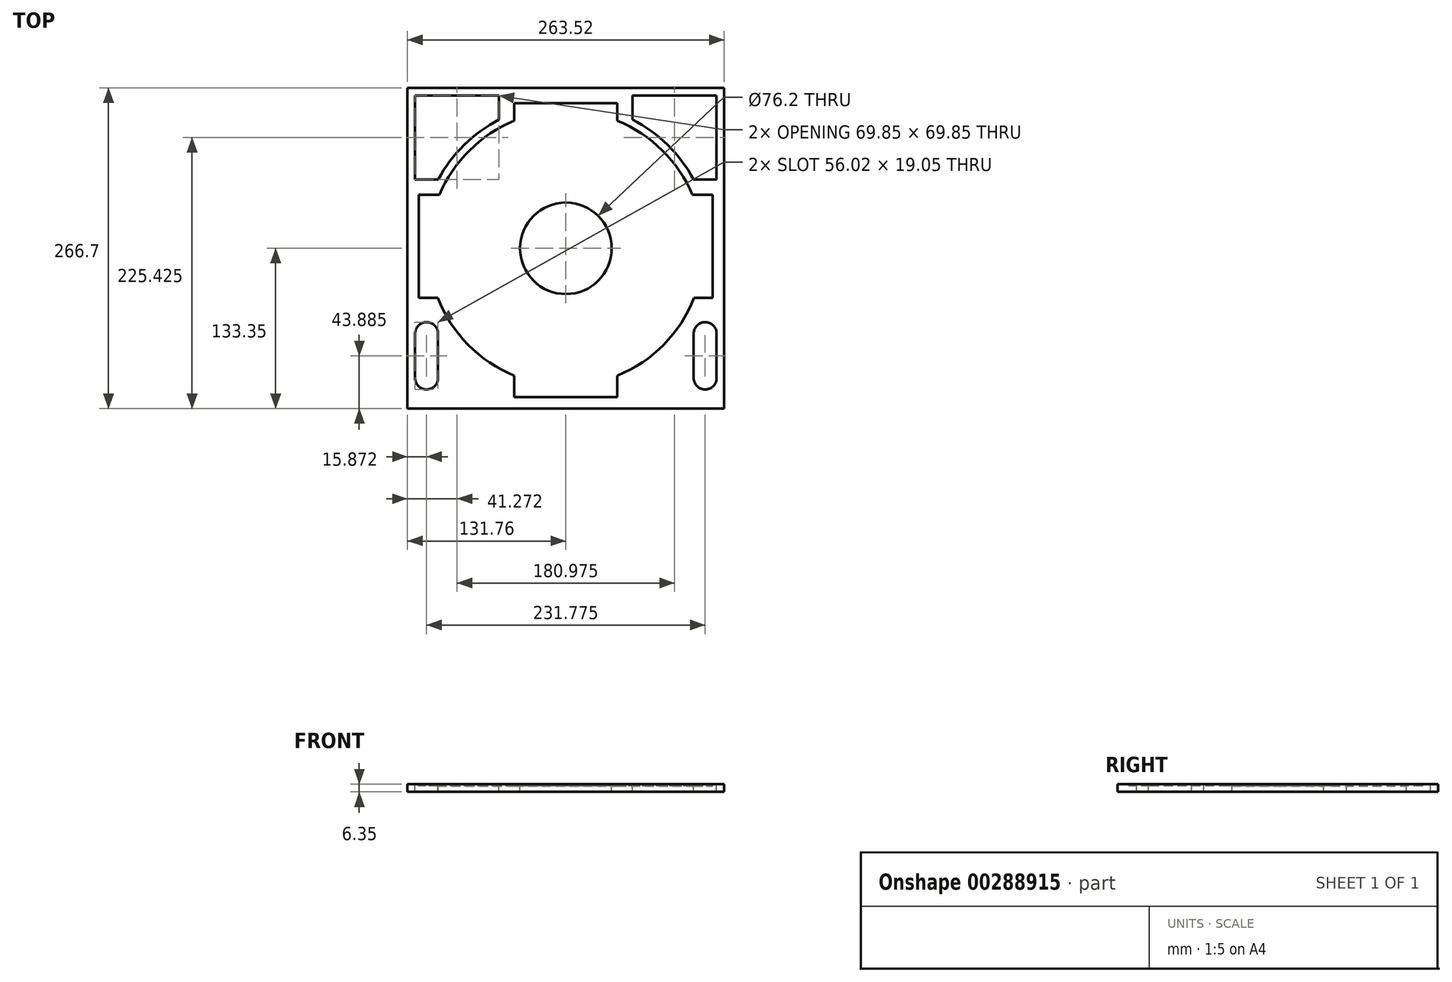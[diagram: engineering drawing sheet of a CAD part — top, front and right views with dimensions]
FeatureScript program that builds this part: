
annotation { "Feature Type Name" : "Feature", "Feature Type Description" : "" }
export const myFeature = defineFeature(function(context is Context, id is Id, definition is map)
    precondition{}
    {
        {
            var Q0;
            Q0=qCreatedBy(makeId("Top.planeOp"),FACE);
            var sketch = newSketch(context, id + "F0", { "sketchPlane" : qUnion([Q0])});
            skLineSegment(sketch, "E0.bottom", {"start": v(-134.94, -136.53) * mm, "end": v(134.94, -136.53) * mm});
            skLineSegment(sketch, "E0.top", {"start": v(-134.94, 136.53) * mm, "end": v(134.94, 136.53) * mm});
            skLineSegment(sketch, "E0.left", {"start": v(-134.94, -136.53) * mm, "end": v(-134.94, 136.53) * mm});
            skLineSegment(sketch, "E0.right", {"start": v(134.94, -136.53) * mm, "end": v(134.94, 136.53) * mm});
            skPoint(sketch, "E0.middle", {"position": v(0, 0) * mm});
            skSolve(sketch);
        }
        {
            var Q0;
            Q0 = qSketchRegion(id + "F0", true);
            extrude(context, id + "F1", {"entities" : qUnion([Q0]), "depth" : 6.35 * mm});
        }
        {
            var Q0;
            Q0=makeQuery(id+"F1.opExtrude","CAP_FACE",FACE,{"disambiguationData":[OSD([sQuery(id+"F0.wireOp",EDGE,"E0.bottom"),sQuery(id+"F0.wireOp",EDGE,"E0.top"),sQuery(id+"F0.wireOp",EDGE,"E0.left"),sQuery(id+"F0.wireOp",EDGE,"E0.right")])],"isStart":false});
            var sketch = newSketch(context, id + "F2", { "sketchPlane" : qUnion([Q0])});
            skLineSegment(sketch, "E1", {"start": v(-125.41, 136.53) * mm, "end": v(-125.41, -136.53) * mm, "construction": true});
            skLineSegment(sketch, "E2", {"start": v(125.41, 136.53) * mm, "end": v(125.41, -136.53) * mm, "construction": true});
            skLineSegment(sketch, "E3", {"start": v(-134.94, 127) * mm, "end": v(134.94, 127) * mm, "construction": true});
            skLineSegment(sketch, "E4", {"start": v(-134.94, -117.48) * mm, "end": v(134.94, -117.48) * mm, "construction": true});
            skLineSegment(sketch, "E5", {"start": v(-134.94, 136.53) * mm, "end": v(134.94, -136.53) * mm, "construction": true});
            skLineSegment(sketch, "E6", {"start": v(134.94, -107.94) * mm, "end": v(125.41, -107.94) * mm, "construction": true});
            skLineSegment(sketch, "E7", {"start": v(134.94, -71) * mm, "end": v(125.41, -71) * mm, "construction": true});
            skLineSegment(sketch, "E8", {"start": v(-134.94, -61.46) * mm, "end": v(134.94, -61.46) * mm, "construction": true});
            skLineSegment(sketch, "E9", {"start": v(-125.41, 127) * mm, "end": v(-125.41, 57.15) * mm});
            skLineSegment(sketch, "E10", {"start": v(-125.41, 57.15) * mm, "end": v(-106.25, 57.15) * mm});
            skLineSegment(sketch, "E11", {"start": v(-125.41, 127) * mm, "end": v(-55.56, 127) * mm});
            skLineSegment(sketch, "E12", {"start": v(-55.56, 127) * mm, "end": v(-55.56, 107.09) * mm});
            skLineSegment(sketch, "E13", {"start": v(55.56, 107.09) * mm, "end": v(55.56, 127) * mm});
            skLineSegment(sketch, "E14", {"start": v(55.56, 127) * mm, "end": v(125.41, 127) * mm});
            skLineSegment(sketch, "E15", {"start": v(125.41, 127) * mm, "end": v(125.41, 57.15) * mm});
            skLineSegment(sketch, "E16", {"start": v(125.41, 57.15) * mm, "end": v(106.25, 57.15) * mm});
            skArc(sketch, "E17.trimOffspring", {"start": v(106.25, 57.15) * mm, "mid": v(84.67, 85.94) * mm, "end": v(55.56, 107.09) * mm});
            skArc(sketch, "E18.trimOffspring", {"start": v(-55.56, 107.09) * mm, "mid": v(-84.67, 85.94) * mm, "end": v(-106.25, 57.15) * mm});
            skLineSegment(sketch, "E19", {"start": v(-106.36, 136.53) * mm, "end": v(-106.36, -136.53) * mm, "construction": true});
            skLineSegment(sketch, "E20", {"start": v(106.36, 136.53) * mm, "end": v(106.36, -136.53) * mm, "construction": true});
            skLineSegment(sketch, "E21", {"start": v(-125.41, -71) * mm, "end": v(-125.41, -107.94) * mm});
            skLineSegment(sketch, "E22", {"start": v(-106.36, -107.94) * mm, "end": v(-106.36, -71) * mm});
            skArc(sketch, "E23", {"start": v(-106.36, -71.49) * mm, "mid": v(-115.89, -61.46) * mm, "end": v(-125.41, -71.49) * mm});
            skArc(sketch, "E24", {"start": v(-125.41, -107.45) * mm, "mid": v(-115.89, -117.48) * mm, "end": v(-106.36, -107.45) * mm});
            skLineSegment(sketch, "E25.trimOffspring", {"start": v(-125.41, -71) * mm, "end": v(-134.94, -71) * mm, "construction": true});
            skLineSegment(sketch, "E26.trimOffspring", {"start": v(-125.41, -107.94) * mm, "end": v(-134.94, -107.94) * mm, "construction": true});
            skLineSegment(sketch, "E27", {"start": v(106.36, -71) * mm, "end": v(106.36, -107.94) * mm});
            skLineSegment(sketch, "E28", {"start": v(106.36, -107.94) * mm, "end": v(106.68, -107.94) * mm});
            skLineSegment(sketch, "E29", {"start": v(125.41, -107.94) * mm, "end": v(125.41, -71) * mm});
            skArc(sketch, "E30", {"start": v(125.41, -71.48) * mm, "mid": v(115.89, -61.46) * mm, "end": v(106.36, -71.48) * mm});
            skArc(sketch, "E31", {"start": v(106.36, -107.45) * mm, "mid": v(115.89, -117.48) * mm, "end": v(125.41, -107.45) * mm});
            skLineSegment(sketch, "E32.trimOffspring", {"start": v(106.36, -71) * mm, "end": v(-106.36, -71) * mm, "construction": true});
            skLineSegment(sketch, "E33.trimOffspring", {"start": v(106.68, -107.94) * mm, "end": v(-106.36, -107.94) * mm, "construction": true});
            skSolve(sketch);
        }
        {
            var Q0;
            Q0 = qSketchRegion(id + "F2", true);
            extrude(context, id + "F3", {"entities" : qUnion([Q0]), "operationType" : NewBodyOperationType.REMOVE, "endBound" : BoundingType.UP_TO_NEXT, "oppositeDirection" : true, "depth" : 25.4 * mm});
        }
        {
            var Q0;
            Q0=makeQuery(id+"F1.opExtrude","CAP_FACE",FACE,{"disambiguationData":[OSD([sQuery(id+"F0.wireOp",EDGE,"E0.bottom"),sQuery(id+"F0.wireOp",EDGE,"E0.top"),sQuery(id+"F0.wireOp",EDGE,"E0.left"),sQuery(id+"F0.wireOp",EDGE,"E0.right")])],"isStart":false});
            var sketch = newSketch(context, id + "F4", { "sketchPlane" : qUnion([Q0])});
            skLineSegment(sketch, "E34", {"start": v(-134.94, 136.53) * mm, "end": v(134.94, -136.53) * mm, "construction": true});
            skCircle(sketch, "E35", {"center": v(0, 0) * mm, "radius": 38.1 * mm});
            skSolve(sketch);
        }
        {
            var Q0;
            Q0 = qSketchRegion(id + "F4", true);
            extrude(context, id + "F5", {"entities" : qUnion([Q0]), "operationType" : NewBodyOperationType.REMOVE, "endBound" : BoundingType.UP_TO_NEXT, "oppositeDirection" : true, "depth" : 25.4 * mm});
        }
        {
            var Q0;
            Q0=makeQuery(id+"F1.opExtrude","CAP_FACE",FACE,{"disambiguationData":[OSD([sQuery(id+"F0.wireOp",EDGE,"E0.bottom"),sQuery(id+"F0.wireOp",EDGE,"E0.top"),sQuery(id+"F0.wireOp",EDGE,"E0.left"),sQuery(id+"F0.wireOp",EDGE,"E0.right")])],"isStart":false});
            var sketch = newSketch(context, id + "F6", { "sketchPlane" : qUnion([Q0])});
            skLineSegment(sketch, "E36", {"start": v(-134.94, 136.53) * mm, "end": v(134.94, -136.53) * mm, "construction": true});
            skCircle(sketch, "E37", {"center": v(0, 0) * mm, "radius": 114.3 * mm});
            skLineSegment(sketch, "E38", {"start": v(0, 136.53) * mm, "end": v(0, -136.53) * mm, "construction": true});
            skLineSegment(sketch, "E39", {"start": v(-134.94, 0) * mm, "end": v(134.94, 0) * mm, "construction": true});
            skLineSegment(sketch, "E40", {"start": v(-55.56, 136.53) * mm, "end": v(-55.56, -136.53) * mm, "construction": true});
            skLineSegment(sketch, "E41", {"start": v(55.56, 136.53) * mm, "end": v(55.56, -136.53) * mm, "construction": true});
            skLineSegment(sketch, "E42", {"start": v(-134.94, 57.15) * mm, "end": v(134.94, 57.15) * mm, "construction": true});
            skLineSegment(sketch, "E43", {"start": v(-106.59, -41.28) * mm, "end": v(-42.86, -41.28) * mm, "construction": true});
            skLineSegment(sketch, "E44", {"start": v(-42.86, 136.53) * mm, "end": v(-42.86, 43.37) * mm, "construction": true});
            skLineSegment(sketch, "E45", {"start": v(42.86, 136.53) * mm, "end": v(42.86, 44.45) * mm, "construction": true});
            skLineSegment(sketch, "E46", {"start": v(-134.94, 127) * mm, "end": v(134.94, 127) * mm, "construction": true});
            skLineSegment(sketch, "E47", {"start": v(134.94, 120.65) * mm, "end": v(-134.94, 120.65) * mm, "construction": true});
            skLineSegment(sketch, "E48", {"start": v(-134.94, -123.83) * mm, "end": v(134.94, -123.83) * mm, "construction": true});
            skLineSegment(sketch, "E49.bottom", {"start": v(-42.86, 120.65) * mm, "end": v(42.86, 120.65) * mm});
            skLineSegment(sketch, "E49.top", {"start": v(-42.86, -123.83) * mm, "end": v(42.86, -123.83) * mm});
            skLineSegment(sketch, "E49.left", {"start": v(-42.86, 120.65) * mm, "end": v(-42.86, 44.45) * mm});
            skLineSegment(sketch, "E49.right", {"start": v(42.86, 120.65) * mm, "end": v(42.86, 44.45) * mm});
            skLineSegment(sketch, "E50", {"start": v(-105.3, 44.45) * mm, "end": v(-42.86, 44.45) * mm, "construction": true});
            skLineSegment(sketch, "E51.bottom", {"start": v(-105.3, 44.45) * mm, "end": v(-42.86, 44.45) * mm});
            skLineSegment(sketch, "E51.top", {"start": v(-106.59, -41.28) * mm, "end": v(-42.86, -41.28) * mm});
            skLineSegment(sketch, "E52.trimOffspring", {"start": v(42.86, 44.45) * mm, "end": v(55.56, 44.45) * mm, "construction": true});
            skLineSegment(sketch, "E53.trimOffspring", {"start": v(42.86, 44.45) * mm, "end": v(105.3, 44.45) * mm});
            skLineSegment(sketch, "E54.trimOffspring", {"start": v(42.86, -41.28) * mm, "end": v(42.86, -136.53) * mm, "construction": true});
            skLineSegment(sketch, "E55.trimOffspring", {"start": v(42.86, -41.28) * mm, "end": v(42.86, -123.83) * mm});
            skLineSegment(sketch, "E56.trimOffspring", {"start": v(40.8, -41.28) * mm, "end": v(106.59, -41.28) * mm, "construction": true});
            skLineSegment(sketch, "E57.trimOffspring", {"start": v(40.8, -41.28) * mm, "end": v(106.59, -41.28) * mm});
            skLineSegment(sketch, "E58.trimOffspring", {"start": v(-42.86, -41.28) * mm, "end": v(-42.86, -136.53) * mm, "construction": true});
            skLineSegment(sketch, "E59.trimOffspring", {"start": v(-42.86, -41.28) * mm, "end": v(-42.86, -123.83) * mm});
            skLineSegment(sketch, "E60", {"start": v(-122.24, 136.53) * mm, "end": v(-122.24, -136.53) * mm, "construction": true});
            skLineSegment(sketch, "E61", {"start": v(122.24, 136.53) * mm, "end": v(122.24, -136.53) * mm, "construction": true});
            skLineSegment(sketch, "E62", {"start": v(105.3, 44.45) * mm, "end": v(122.24, 44.45) * mm});
            skLineSegment(sketch, "E63", {"start": v(106.59, -41.28) * mm, "end": v(122.24, -41.28) * mm});
            skLineSegment(sketch, "E64", {"start": v(122.24, -41.28) * mm, "end": v(122.24, 44.45) * mm});
            skLineSegment(sketch, "E65", {"start": v(-106.59, -41.28) * mm, "end": v(-122.24, -41.28) * mm});
            skLineSegment(sketch, "E66", {"start": v(-105.3, 44.45) * mm, "end": v(-122.24, 44.45) * mm});
            skLineSegment(sketch, "E67", {"start": v(-122.24, 44.45) * mm, "end": v(-122.24, -41.28) * mm});
            skSolve(sketch);
        }
        {
            var Q0;
            Q0 = qSketchRegion(id + "F6", true);
            extrude(context, id + "F7", {"entities" : qUnion([Q0]), "operationType" : NewBodyOperationType.REMOVE, "oppositeDirection" : true, "depth" : 1.59 * mm});
        }
        {
            var Q0;
            Q0=makeQuery(id+"F1.opExtrude","CAP_FACE",FACE,{"disambiguationData":[OSD([sQuery(id+"F0.wireOp",EDGE,"E0.bottom"),sQuery(id+"F0.wireOp",EDGE,"E0.top"),sQuery(id+"F0.wireOp",EDGE,"E0.left"),sQuery(id+"F0.wireOp",EDGE,"E0.right")])],"isStart":false});
            var sketch = newSketch(context, id + "F8", { "sketchPlane" : qUnion([Q0])});
            skLineSegment(sketch, "E68.bottom", {"start": v(-134.94, -136.53) * mm, "end": v(-131.76, -136.53) * mm});
            skLineSegment(sketch, "E68.top", {"start": v(-134.94, 136.53) * mm, "end": v(-131.76, 136.53) * mm});
            skLineSegment(sketch, "E68.left", {"start": v(-134.94, -136.53) * mm, "end": v(-134.94, 136.53) * mm});
            skLineSegment(sketch, "E68.right", {"start": v(-131.76, -136.53) * mm, "end": v(-131.76, 136.53) * mm});
            skLineSegment(sketch, "E69.bottom", {"start": v(134.94, 136.53) * mm, "end": v(131.76, 136.53) * mm});
            skLineSegment(sketch, "E69.top", {"start": v(134.94, -136.53) * mm, "end": v(131.76, -136.53) * mm});
            skLineSegment(sketch, "E69.left", {"start": v(134.94, 136.53) * mm, "end": v(134.94, -136.53) * mm});
            skLineSegment(sketch, "E69.right", {"start": v(131.76, 136.53) * mm, "end": v(131.76, -136.53) * mm});
            skSolve(sketch);
        }
        {
            var Q0;
            Q0 = qSketchRegion(id + "F8", true);
            extrude(context, id + "F9", {"entities" : qUnion([Q0]), "operationType" : NewBodyOperationType.REMOVE, "endBound" : BoundingType.UP_TO_NEXT, "oppositeDirection" : true, "depth" : 25.4 * mm});
        }
        {
            var Q0;
            Q0=makeQuery(id+"F1.opExtrude","CAP_FACE",FACE,{"disambiguationData":[OSD([sQuery(id+"F0.wireOp",EDGE,"E0.bottom"),sQuery(id+"F0.wireOp",EDGE,"E0.top"),sQuery(id+"F0.wireOp",EDGE,"E0.left"),sQuery(id+"F0.wireOp",EDGE,"E0.right")])],"isStart":false});
            var sketch = newSketch(context, id + "F10", { "sketchPlane" : qUnion([Q0])});
            skLineSegment(sketch, "E70.bottom", {"start": v(-131.76, 136.53) * mm, "end": v(131.76, 136.53) * mm});
            skLineSegment(sketch, "E70.top", {"start": v(-131.76, 133.35) * mm, "end": v(131.76, 133.35) * mm});
            skLineSegment(sketch, "E70.left", {"start": v(-131.76, 136.53) * mm, "end": v(-131.76, 133.35) * mm});
            skLineSegment(sketch, "E70.right", {"start": v(131.76, 136.53) * mm, "end": v(131.76, 133.35) * mm});
            skSolve(sketch);
        }
        {
            var Q0;
            Q0 = qSketchRegion(id + "F10", true);
            extrude(context, id + "F11", {"entities" : qUnion([Q0]), "operationType" : NewBodyOperationType.REMOVE, "endBound" : BoundingType.UP_TO_NEXT, "oppositeDirection" : true, "depth" : 25.4 * mm});
        }
        {
            var Q0;
            Q0=makeQuery(id+"F1.opExtrude","CAP_FACE",FACE,{"disambiguationData":[OSD([sQuery(id+"F0.wireOp",EDGE,"E0.bottom"),sQuery(id+"F0.wireOp",EDGE,"E0.top"),sQuery(id+"F0.wireOp",EDGE,"E0.left"),sQuery(id+"F0.wireOp",EDGE,"E0.right")])],"isStart":false});
            var sketch = newSketch(context, id + "F12", { "sketchPlane" : qUnion([Q0])});
            skLineSegment(sketch, "E71.bottom", {"start": v(-131.76, -136.53) * mm, "end": v(131.76, -136.53) * mm});
            skLineSegment(sketch, "E71.top", {"start": v(-131.76, -133.35) * mm, "end": v(131.76, -133.35) * mm});
            skLineSegment(sketch, "E71.left", {"start": v(-131.76, -136.53) * mm, "end": v(-131.76, -133.35) * mm});
            skLineSegment(sketch, "E71.right", {"start": v(131.76, -136.53) * mm, "end": v(131.76, -133.35) * mm});
            skSolve(sketch);
        }
        {
            var Q0;
            Q0 = qSketchRegion(id + "F12", true);
            extrude(context, id + "F13", {"entities" : qUnion([Q0]), "operationType" : NewBodyOperationType.REMOVE, "endBound" : BoundingType.UP_TO_NEXT, "oppositeDirection" : true, "depth" : 25.4 * mm});
        }
    });
